# Revit family: EDE-GRF-DCH_Doccia Centerset 4 para Lavamanos Cromo
name_source: partatom
category: Aparatos sanitarios
units: mm (PartAtom-declared; Revit-internal decimal feet)

## family parameters
Compartido = Sí
Corte con vacíos al cargar = No
Cota de conector redondo = Diámetro de uso
Número OmniClass = 23.45.00.00
Punto de cálculo de habitación = Sí
Se basa en plano de trabajo = No
Siempre vertical = Sí
Tipo de pieza = Normal
Título OmniClass = Sanitary, Laundry, and Cleaning Equipment

## types (1)
- DOCCIA CENTERSET 4" PARA LAVAMANOS
    Conexión AC = Sí
    Conexión AF = Sí
    Conexión de residuos = Sí
    Conexión de ventilación = Sí
    Fabricante = BRIGGS Ecuador
    Imagen de tipo = <Ninguno>
    Modelo = DOCCIA CENTERSET 4" PARA LAVAMANOS
    URL = https://www.edesa.com.ec
    _ALT_Meson = 0.85 m
    _ALT_Toma = 0.55 m
    _EDESA_ Alto en cm = 7.5
    _EDESA_ Ancho en cm = 15.5
    _EDESA_ Categoría = Productos > Grifería > Lavamanos
    _EDESA_ Certificación = Cumple con norma NTE - INEN 3123 basada en la norma ASME 112.18.1 - 2012.
    _EDESA_ Color = cromo
    _EDESA_ Conexión hidráulica = Entrada de agua: tubería ø 1/2" Salida de agua: tubería PVC 50
    _EDESA_ Consumo/capacidad de agua en L = 8.3 litros por minuto / 2.2 gpm a 60 psi
    _EDESA_ Descripción = Grifería bimando 4" de lavamanos para agua fría y caliente. Instalación sobre lavamanos.
    _EDESA_ Garantía = De por vida para el cuerpo principal y acabado en cromo (306)
    _EDESA_ Manual de instalación = https://www.edesa.com.ec
    _EDESA_ Marca = EDESA
    _EDESA_ Materiales = ABS cromado
    _EDESA_ Nombre = DOCCIA CENTERSET 4" PARA LAVAMANOS
    _EDESA_ Productos necesarios para instalación = Desagüe 1 1/4", Sifón 1 1/4", Llaves Angulares y Mangueras Flexibles
    _EDESA_ Profundidad en cm = 15
    _EDESA_ Sku/código = SG0063373061CE
    _EDESA_ Tipo de instalación = Sobre lavamanos
